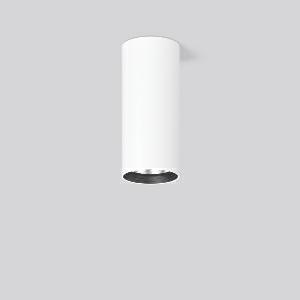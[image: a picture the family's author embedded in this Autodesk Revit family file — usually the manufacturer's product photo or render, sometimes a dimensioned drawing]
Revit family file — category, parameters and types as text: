
# Revit family: heledon_mini_a_931202_002_1_87b4
name_source: partatom
category: Lighting Fixtures
units: mm (PartAtom-declared; Revit-internal decimal feet)

## family parameters
Cut with Voids When Loaded = No
Host = Face
Light Source = No
Part Type = Normal
Room Calculation Point = No
Round Connector Dimension = Use Diameter
Shared = No

## types (1)
- HELEDON mini A (1 x LED Modul 940, 2750 lm, 4000)
    Apparent Load = 20 VA
    Approval mark = CE
    CIE Flux Codes = 95 99 100 100 100
    Color Rendering = 92
    Color Temperature = 4000
    Default Elevation = 1800 mm
    Description = Series: HELEDON mini
Cylindrical surface-mounted downlight. Housing: die-cast aluminium, powder-coated. Internal ceiling frame polycarbonate with bayonet mounting. Black plastic ring and recessed LED to prevent glare from the side. Optical assembly with reflector made of MIRO-Silver with 98% total light reflection for outstanding efficiency - can be changed without tools. Best colour rendering index Ra>90. Suitable for Ceiling mounting. Easy installation with a separate ceiling frame with bayonet mounting and plug connection. Driver integrated. Connected via plug-in connector. High quality converter without flickering and stroboscopic effect. The following accessories can be mounted without use of tools: interchangeable lenses, decorative glasses, honeycomb louvre, clear and frosted diffusers, white interchangeable plastic ring. 
Colour: traffic white, matt (RAL 9016)
Diameter: 87 mm
Height: 197 mm
Lamp: LED
Socket: without socket
Colour temperature: 4000K
Colour rendering index (CRI): 92
System power: 20 W
Rated luminous flux: 2750 lm
Luminous efficiency: 138 lm/W
Control gear: Regulated power supply
Protection class: I
Type of protection: IP 20
    Height = 197 mm
    Lamp = 1 x LED Modul 940
    Lamp Light Flux = 2750 lm
    Lamp count = 1
    Length = 87 mm
    Lifetime = 50000 h
    Luminous efficacy = 138 lm/W
    Manufacturer = RZB
    ModVariant = No
    Model = 931202.002.1
    Mounting Place = Ceiling
    Mounting Type = Surface mounted
    Number of Poles = 1
    OnlyDefault = Yes
    Power Factor = 1
    Product Name = HELEDON mini A
    Product group = Surface mounted downlights
    ProductGroupID = 302
    Protection Class = Protection class I
    Protection Degree = IP 20
    RLX_Detail_Level = 1
    RLX_Emergency_Light_Flux = 0 lm
    RLX_Emergency_Type = 0
    RLX_Emergency_Type_DB = No
    RlxData = <blob elided: 104853 chars, md5=d46a27a2>
    Socket = socket
    Standby Power = 0 W
    System Light Flux = 2750 lm
    System Power = 20 W
    Type Comments = Product without accessories
    Type Image = 931188.002.jpg
    URL = http://relux.com
    VarID = ---
    Voltage = 230 V
    Voltage Range = 220-240 V
    Weight = 0.00 kg
    Width = 0 mm  [stored 0 ft]

note: [stored X ft] marks values corroborated as IEEE doubles in the binary element streams (Revit-internal decimal feet)

## geometry (parser evidence)
native form markers: Blend x4, Sweep x10
no freeform markers — native parametric forms only
